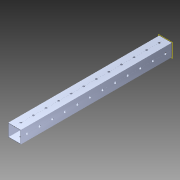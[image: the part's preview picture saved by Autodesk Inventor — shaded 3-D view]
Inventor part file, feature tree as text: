
AUTODESK INVENTOR PART (.ipt)
format: ipt  version: 2014 (Build 180170000, 170)  size: 1,175,040 bytes
history: native  units: in
note: dims shown in document units (in); Inventor stores cm internally (conversion verified against a paired STEP export)
features: pattern_circular x1, other x1, plane x1, extrude x1, imported_body x1, sketch x1
ambient origin geometry x8: Origin, YZ Plane, XZ Plane, XY Plane, X Axis, Y Axis, Z Axis, Center Point
bodies: Body1 (feature_tree)
feature tree (6):
  pattern_circular  "CirPattern2"
  other  "217-3426-STEP1"
  plane  "Work Plane1"
  extrude  "Extrusion1"  Depth=3937.0079in TaperAngle=0.0deg
  imported_body  "Base1"
  sketch  "Sketch1"  dims[d0=-12.0in d1=3937.0079in d2=0.0in]
